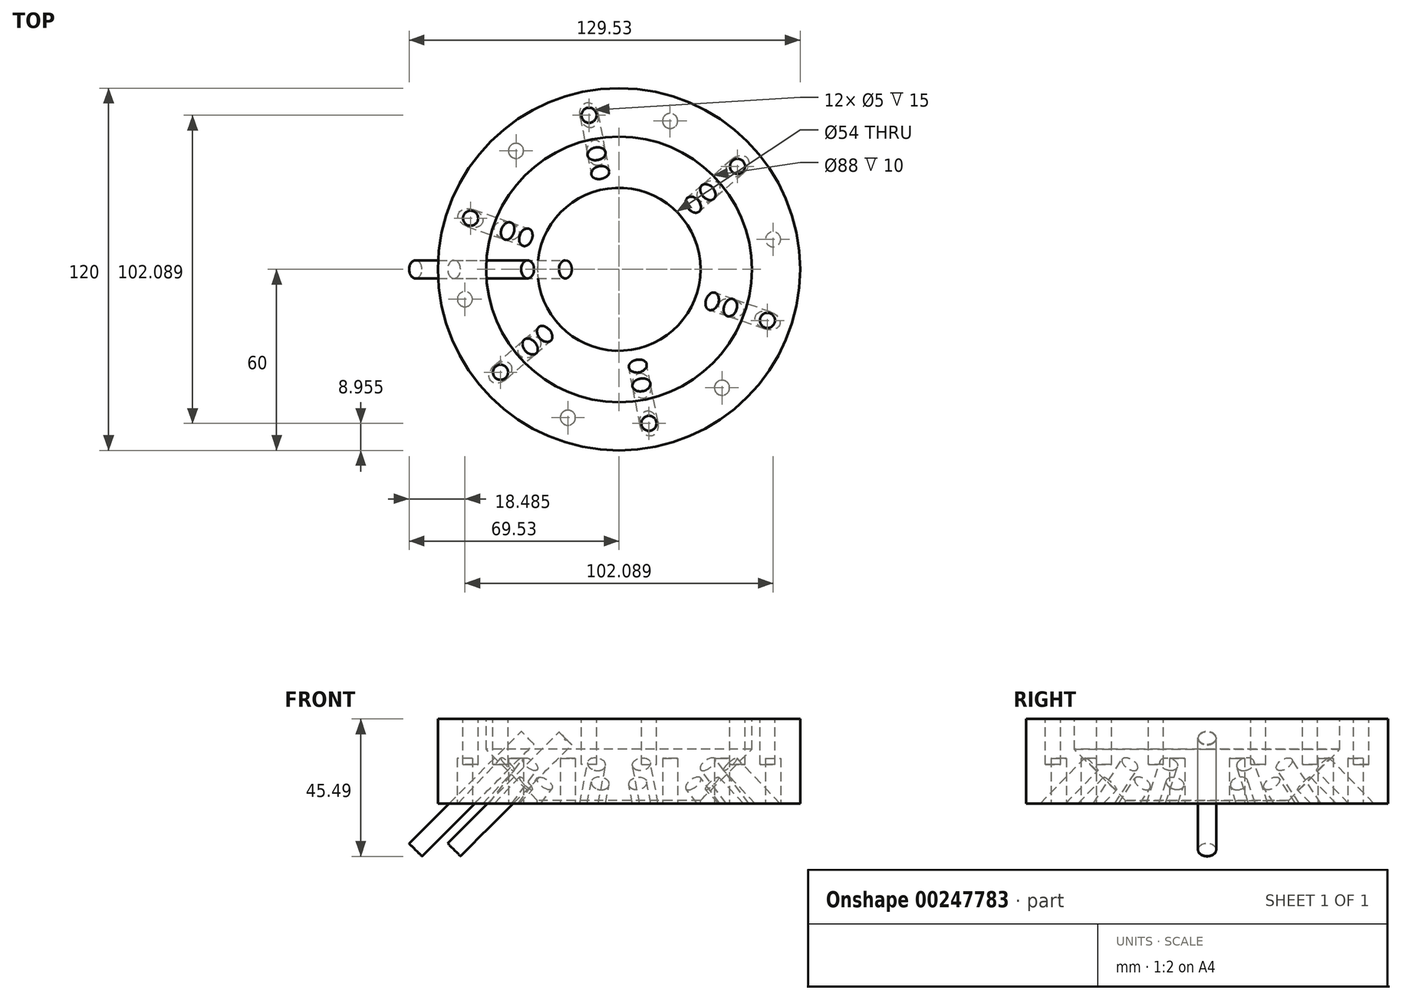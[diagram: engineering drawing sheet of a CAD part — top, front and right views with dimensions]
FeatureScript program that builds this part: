
annotation { "Feature Type Name" : "Feature", "Feature Type Description" : "" }
export const myFeature = defineFeature(function(context is Context, id is Id, definition is map)
    precondition{}
    {
        {
            var Q0;
            Q0=qCreatedBy(makeId("Front.planeOp"),FACE);
            var sketch = newSketch(context, id + "F0", { "sketchPlane" : qUnion([Q0])});
            skLineSegment(sketch, "E0", {"start": v(0, 70.12) * mm, "end": v(0, -51.14) * mm, "construction": true});
            skLineSegment(sketch, "E1", {"start": v(-40, -25.13) * mm, "end": v(-40, -82.12) * mm, "construction": true});
            skLineSegment(sketch, "E2", {"start": v(-33.5, -13) * mm, "end": v(-33.5, -83.09) * mm, "construction": true});
            skLineSegment(sketch, "E3", {"start": v(-55, -23.79) * mm, "end": v(-55, -71.7) * mm, "construction": true});
            skPoint(sketch, "E4", {"position": v(-45, -20) * mm});
            skLineSegment(sketch, "E5", {"start": v(-27, -2) * mm, "end": v(-44, 15) * mm});
            skLineSegment(sketch, "E6", {"start": v(-44, 20) * mm, "end": v(0, 20) * mm, "construction": true});
            skLineSegment(sketch, "E7.trimOffspring", {"start": v(-44, 15) * mm, "end": v(-44, 25) * mm});
            skLineSegment(sketch, "E8", {"start": v(0, 20) * mm, "end": v(0, -2) * mm});
            skLineSegment(sketch, "E9", {"start": v(-15, -3) * mm, "end": v(-15, -14) * mm});
            skLineSegment(sketch, "E10.trimOffspring", {"start": v(-44, 25) * mm, "end": v(-60, 25) * mm});
            skLineSegment(sketch, "E11", {"start": v(-27, -14) * mm, "end": v(-60, -14) * mm, "construction": true});
            skLineSegment(sketch, "E12", {"start": v(-44, -3) * mm, "end": v(-26, -3) * mm});
            skLineSegment(sketch, "E13", {"start": v(-60.56, -2) * mm, "end": v(-7.47, -2) * mm, "construction": true});
            skLineSegment(sketch, "E14", {"start": v(-32.2, -0.13) * mm, "end": v(-20.33, 11.74) * mm, "construction": true});
            skLineSegment(sketch, "E15", {"start": v(-37.48, 3.07) * mm, "end": v(-25.45, 15.1) * mm, "construction": true});
            skLineSegment(sketch, "E16", {"start": v(-39.45, 6.77) * mm, "end": v(-29.58, 16.63) * mm, "construction": true});
            skLineSegment(sketch, "E17", {"start": v(-44.65, 10.05) * mm, "end": v(-35.06, 19.64) * mm, "construction": true});
            skPoint(sketch, "E18", {"position": v(-27, -2) * mm});
            skLineSegment(sketch, "E19", {"start": v(-27, -2) * mm, "end": v(-16.61, 8.39) * mm, "construction": true});
            skLineSegment(sketch, "E20", {"start": v(-60, 25) * mm, "end": v(-60, -3) * mm});
            skLineSegment(sketch, "E21", {"start": v(-27, -2) * mm, "end": v(-27, -3) * mm});
            skLineSegment(sketch, "E22", {"start": v(-44, -3) * mm, "end": v(-44, -3) * mm});
            skLineSegment(sketch, "E23", {"start": v(-67.6, -3) * mm, "end": v(-41.15, -3) * mm});
            skSolve(sketch);
        }
        {
            var Q0;
            Q0=makeQuery(id+"F0.imprint","IMPRINT",FACE,{"disambiguationData":[TD([[makeQuery(id+"F0.imprint","IMPRINT",EDGE,{"derivedFrom":sQuery(id+"F0.wireOp",EDGE,"E5")}),1.0]])]});
            var Q1;
            Q1=sQuery(id+"F0.wireOp",EDGE,"E8");
            revolve(context, id + "F1", {"entities" : qUnion([Q0]), "axis" : qUnion([Q1]), "revolveType" : RevolveType.FULL});
        }
        {
            var Q0;
            Q0=qCreatedBy(makeId("Front.planeOp"),FACE);
            var sketch = newSketch(context, id + "F2", { "sketchPlane" : qUnion([Q0])});
            skLineSegment(sketch, "E24.0", {"start": v(-55, -23.79) * mm, "end": v(-55, -71.7) * mm, "construction": true});
            skLineSegment(sketch, "E25.0", {"start": v(-33.5, -13) * mm, "end": v(-33.5, -83.09) * mm, "construction": true});
            skLineSegment(sketch, "E26", {"start": v(-30.26, 18.78) * mm, "end": v(-67.4, -18.36) * mm});
            skLineSegment(sketch, "E27", {"start": v(-32.38, 20.9) * mm, "end": v(-30.26, 18.78) * mm});
            skLineSegment(sketch, "E28", {"start": v(-69.53, -16.24) * mm, "end": v(-67.4, -18.36) * mm});
            skLineSegment(sketch, "E29.0", {"start": v(-27, -2) * mm, "end": v(-44, 15) * mm});
            skLineSegment(sketch, "E30.0", {"start": v(-27, -2) * mm, "end": v(-16.61, 8.39) * mm, "construction": true});
            skLineSegment(sketch, "E31", {"start": v(-32.38, 20.9) * mm, "end": v(-69.53, -16.24) * mm});
            skSolve(sketch);
        }
        {
            var Q0;
            Q0=qSketchRegion(id+"F2",true);
            var Q1;
            Q1=sQuery(id+"F2.wireOp",EDGE,"E26");
            revolve(context, id + "F3", {"entities" : qUnion([Q0]), "axis" : qUnion([Q1]), "revolveType" : RevolveType.FULL});
        }
        {
            var Q0;
            Q0=makeQuery(id+"F3.opRevolve","SWEPT_BODY",BODY,{"disambiguationData":[OSD([sQuery(id+"F2.wireOp",EDGE,"8dca1c6b-01d1-403d-97e6-a70b6a6dedc9.0"),sQuery(id+"F2.wireOp",EDGE,"E26"),sQuery(id+"F2.wireOp",EDGE,"E27"),sQuery(id+"F2.wireOp",EDGE,"BTjxJDAI-CfnJ-hfkt-lCJ7-kgF73TjLmZTi")])]});
            var Q1;
            Q1=sQuery(id+"F0.wireOp",EDGE,"E0");
            circularPattern(context, id + "F4", {"entities" : qUnion([Q0]), "axis" : qUnion([Q1]), "angle" : 19 * degree, "instanceCount" : 2, "equalSpace" : true});
        }
        {
            var Q0;
            Q0=makeQuery(id+"F4.opPattern","COPY",BODY,{"derivedFrom":makeQuery(id+"F3.opRevolve","SWEPT_BODY",BODY,{"disambiguationData":[OSD([sQuery(id+"F2.wireOp",EDGE,"8dca1c6b-01d1-403d-97e6-a70b6a6dedc9.0"),sQuery(id+"F2.wireOp",EDGE,"E26"),sQuery(id+"F2.wireOp",EDGE,"E27"),sQuery(id+"F2.wireOp",EDGE,"BTjxJDAI-CfnJ-hfkt-lCJ7-kgF73TjLmZTi")])]}),"instanceName":"1"});
            var Q1;
            Q1=sQuery(id+"F0.wireOp",EDGE,"E0");
            circularPattern(context, id + "F5", {"operationType" : NewBodyOperationType.REMOVE, "entities" : qUnion([Q0]), "axis" : qUnion([Q1]), "angle" : 360 * degree, "instanceCount" : 6, "equalSpace" : true});
        }
        {
            var Q0;
            Q0=qCreatedBy(makeId("Front.planeOp"),FACE);
            var sketch = newSketch(context, id + "F6", { "sketchPlane" : qUnion([Q0])});
            skLineSegment(sketch, "E32.0", {"start": v(-27, -2) * mm, "end": v(-44, 15) * mm, "construction": true});
            skLineSegment(sketch, "E33", {"start": v(-17.75, 18.57) * mm, "end": v(-54.69, -18.37) * mm});
            skLineSegment(sketch, "E34", {"start": v(-19.87, 20.69) * mm, "end": v(-17.75, 18.57) * mm});
            skLineSegment(sketch, "E35", {"start": v(-56.75, -16.2) * mm, "end": v(-54.63, -18.31) * mm});
            skLineSegment(sketch, "E36", {"start": v(-19.87, 20.69) * mm, "end": v(-56.75, -16.2) * mm});
            skSolve(sketch);
        }
        {
            var Q0;
            Q0=qSketchRegion(id+"F6",true);
            var Q1;
            Q1=sQuery(id+"F6.wireOp",EDGE,"E32.0");
            var Q2;
            Q2=sQuery(id+"F6.wireOp",EDGE,"E33");
            revolve(context, id + "F7", {"entities" : qUnion([Q0]), "surfaceEntities" : qUnion([Q1]), "axis" : qUnion([Q2]), "revolveType" : RevolveType.FULL});
        }
        {
            var Q0;
            Q0=makeQuery(id+"F7.opRevolve","SWEPT_BODY",BODY,{"disambiguationData":[OSD([sQuery(id+"F6.wireOp",EDGE,"0296a30f-b775-46fb-957b-19e912f0fa4b.0"),sQuery(id+"F6.wireOp",EDGE,"E33"),sQuery(id+"F6.wireOp",EDGE,"E34"),sQuery(id+"F6.wireOp",EDGE,"E35")])]});
            var Q1;
            Q1=sQuery(id+"F0.wireOp",EDGE,"E0");
            circularPattern(context, id + "F8", {"entities" : qUnion([Q0]), "axis" : qUnion([Q1]), "angle" : 19 * degree, "instanceCount" : 2, "equalSpace" : true});
        }
        {
            var Q0;
            Q0=makeQuery(id+"F8.opPattern","COPY",BODY,{"derivedFrom":makeQuery(id+"F7.opRevolve","SWEPT_BODY",BODY,{"disambiguationData":[OSD([sQuery(id+"F6.wireOp",EDGE,"0296a30f-b775-46fb-957b-19e912f0fa4b.0"),sQuery(id+"F6.wireOp",EDGE,"E33"),sQuery(id+"F6.wireOp",EDGE,"E34"),sQuery(id+"F6.wireOp",EDGE,"E35")])]}),"instanceName":"1"});
            var Q1;
            Q1=makeQuery(id+"F1.opRevolve","SWEPT_FACE",FACE,{"disambiguationData":[OSD([sQuery(id+"F0.wireOp",EDGE,"E5")])]});
            circularPattern(context, id + "F9", {"operationType" : NewBodyOperationType.REMOVE, "entities" : qUnion([Q0]), "axis" : qUnion([Q1]), "angle" : 360 * degree, "instanceCount" : 6, "equalSpace" : true});
        }
        {
            var Q0;
            Q0=makeQuery(id+"F1.opRevolve","SWEPT_FACE",FACE,{"disambiguationData":[OSD([sQuery(id+"F0.wireOp",EDGE,"E12"),sQuery(id+"F0.wireOp",EDGE,"E23")])]});
            cPlane(context, id + "F10", {"entities" : qUnion([Q0]), "cplaneType" : CPlaneType.OFFSET, "offset" : 0 * mm, "width" : 150 * mm, "height" : 150 * mm});
        }
        {
            var Q0;
            Q0=qCreatedBy(id+"F10.planeOp",FACE);
            var sketch = newSketch(context, id + "F11", { "sketchPlane" : qUnion([Q0])});
            skLineSegment(sketch, "E37", {"start": v(70.55, -13.71) * mm, "end": v(0, 0) * mm, "construction": true});
            skCircle(sketch, "E38", {"center": v(0, 0) * mm, "radius": 52 * mm, "construction": true});
            skCircle(sketch, "E39", {"center": v(51.04, -9.92) * mm, "radius": 2.5 * mm});
            skSolve(sketch);
        }
        {
            var Q0;
            Q0=qSketchRegion(id+"F11",true);
            extrude(context, id + "F12", {"entities" : qUnion([Q0]), "oppositeDirection" : true, "depth" : 15 * mm, "hasSecondDirection" : true, "secondDirectionOppositeDirection" : false, "secondDirectionDepth" : 20 * mm});
        }
        {
            var Q0;
            Q0=makeQuery(id+"F12.opExtrude","SWEPT_BODY",BODY,{"disambiguationData":[OSD([sQuery(id+"F11.wireOp",EDGE,"E39")])]});
            var Q1;
            Q1=sQuery(id+"F0.wireOp",EDGE,"E8");
            circularPattern(context, id + "F13", {"operationType" : NewBodyOperationType.REMOVE, "entities" : qUnion([Q0]), "axis" : qUnion([Q1]), "angle" : 360 * degree, "instanceCount" : 6, "oppositeDirection" : true, "equalSpace" : true});
        }
        {
            var Q0;
            Q0=makeQuery(id+"F1.opRevolve","SWEPT_FACE",FACE,{"disambiguationData":[OSD([sQuery(id+"F0.wireOp",EDGE,"E10.trimOffspring")])]});
            cPlane(context, id + "F14", {"entities" : qUnion([Q0]), "cplaneType" : CPlaneType.OFFSET, "offset" : 0 * mm, "width" : 150 * mm, "height" : 150 * mm});
        }
        {
            var Q0;
            Q0=qCreatedBy(id+"F14.planeOp",FACE);
            var sketch = newSketch(context, id + "F15", { "sketchPlane" : qUnion([Q0])});
            skLineSegment(sketch, "E40", {"start": v(0, 0) * mm, "end": v(-15.23, 78.37) * mm, "construction": true});
            skCircle(sketch, "E41", {"center": v(0, 0) * mm, "radius": 52 * mm, "construction": true});
            skCircle(sketch, "E42", {"center": v(-9.92, 51.04) * mm, "radius": 2.5 * mm});
            skSolve(sketch);
        }
        {
            var Q0;
            Q0=qSketchRegion(id+"F15",true);
            extrude(context, id + "F16", {"entities" : qUnion([Q0]), "oppositeDirection" : true, "depth" : 15 * mm, "hasSecondDirection" : true, "secondDirectionOppositeDirection" : false, "secondDirectionDepth" : 20 * mm});
        }
        {
            var Q0;
            Q0=makeQuery(id+"F16.opExtrude","SWEPT_BODY",BODY,{"disambiguationData":[OSD([sQuery(id+"F15.wireOp",EDGE,"E42")])]});
            var Q1;
            Q1=sQuery(id+"F0.wireOp",EDGE,"E0");
            circularPattern(context, id + "F17", {"operationType" : NewBodyOperationType.REMOVE, "entities" : qUnion([Q0]), "axis" : qUnion([Q1]), "angle" : 360 * degree, "instanceCount" : 6, "equalSpace" : true});
        }
    });
